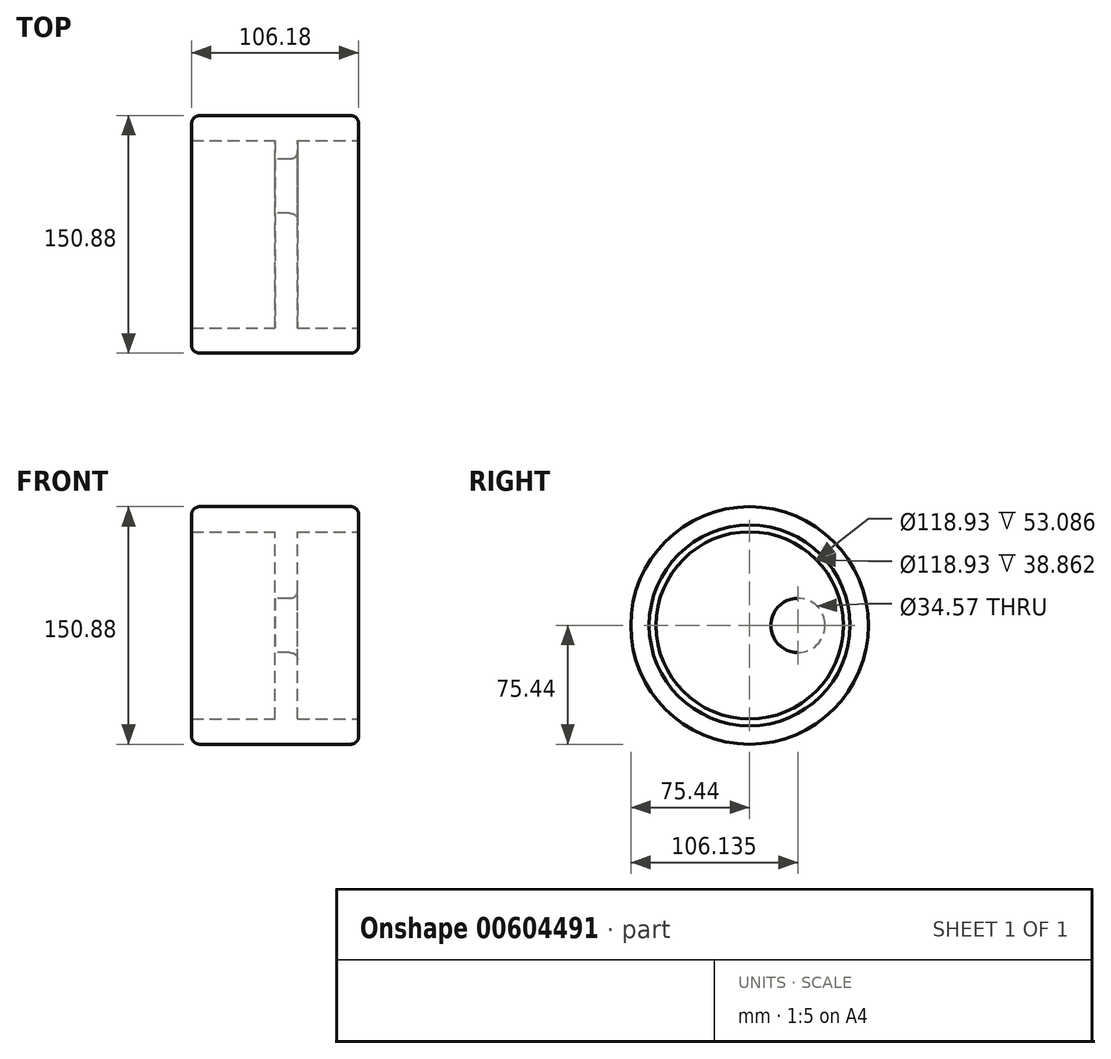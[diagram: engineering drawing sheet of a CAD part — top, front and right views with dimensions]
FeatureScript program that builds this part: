
annotation { "Feature Type Name" : "Feature", "Feature Type Description" : "" }
export const myFeature = defineFeature(function(context is Context, id is Id, definition is map)
    precondition{}
    {
        {
            var Q0;
            Q0=qCreatedBy(makeId("Right.planeOp"),FACE);
            var sketch = newSketch(context, id + "F0", { "sketchPlane" : qUnion([Q0])});
            skCircle(sketch, "E0", {"center": v(0, 0) * mm, "radius": 75.44 * mm});
            skSolve(sketch);
        }
        {
            var Q0;
            Q0 = qSketchRegion(id + "F0", true);
            extrude(context, id + "F1", {"entities" : qUnion([Q0]), "endBound" : BoundingType.SYMMETRIC, "depth" : 106.17 * mm, "offsetDistance" : 25.4 * mm});
        }
        {
            var Q0;
            Q0=makeQuery(id+"F1.opExtrude","SWEPT_FACE",FACE,{"disambiguationData":[OSD([sQuery(id+"F0.wireOp",EDGE,"E0")])]});
            fillet(context, id + "F2", {"entities" : qUnion([Q0]), "radius" : 5.08 * mm, "tangentPropagation" : true, "allowEdgeOverflow" : false});
        }
        {
            var Q0;
            Q0=qCreatedBy(makeId("Right.planeOp"),FACE);
            var sketch = newSketch(context, id + "F3", { "sketchPlane" : qUnion([Q0])});
            skCircle(sketch, "E1", {"center": v(0, 0) * mm, "radius": 58.8 * mm});
            skSolve(sketch);
        }
        {
            var Q0;
            Q0 = qSketchRegion(id + "F3", true);
            extrude(context, id + "F4", {"entities" : qUnion([Q0]), "operationType" : NewBodyOperationType.REMOVE, "endBound" : BoundingType.SYMMETRIC, "oppositeDirection" : true, "depth" : 134.62 * mm, "offsetDistance" : 25.4 * mm});
        }
        {
            var Q0;
            Q0=makeQuery(id+"F4.boolean.opBoolean","INTERSECT",EDGE,{"derivedFrom":[makeQuery(id+"F1.opExtrude","CAP_FACE",FACE,{"disambiguationData":[OSD([sQuery(id+"F0.wireOp",EDGE,"E0")])],"isStart":true}),makeQuery(id+"F4.opExtrude","SWEPT_FACE",FACE,{"disambiguationData":[OSD([sQuery(id+"F3.wireOp",EDGE,"E1")])]})]});
            var Q1;
            Q1=makeQuery(id+"F4.boolean.opBoolean","INTERSECT",EDGE,{"derivedFrom":[makeQuery(id+"F1.opExtrude","CAP_FACE",FACE,{"disambiguationData":[OSD([sQuery(id+"F0.wireOp",EDGE,"E0")])],"isStart":false}),makeQuery(id+"F4.opExtrude","SWEPT_FACE",FACE,{"disambiguationData":[OSD([sQuery(id+"F3.wireOp",EDGE,"E1")])]})]});
            fillet(context, id + "F5", {"entities" : qUnion([Q0, Q1]), "radius" : 5.08 * mm, "tangentPropagation" : true, "allowEdgeOverflow" : false});
        }
        {
            var Q0;
            Q0=qCreatedBy(makeId("Right.planeOp"),FACE);
            var sketch = newSketch(context, id + "F6", { "sketchPlane" : qUnion([Q0])});
            skCircle(sketch, "E2", {"center": v(0, 0) * mm, "radius": 63.75 * mm});
            skSolve(sketch);
        }
        {
            var Q0;
            Q0 = qSketchRegion(id + "F6", true);
            extrude(context, id + "F7", {"entities" : qUnion([Q0]), "operationType" : NewBodyOperationType.ADD, "endBound" : BoundingType.SYMMETRIC, "depth" : 106.17 * mm, "offsetDistance" : 25.4 * mm});
        }
        {
            var Q0;
            Q0=qCreatedBy(makeId("Right.planeOp"),FACE);
            var sketch = newSketch(context, id + "F8", { "sketchPlane" : qUnion([Q0])});
            skCircle(sketch, "E3", {"center": v(0, 0) * mm, "radius": 59.46 * mm});
            skSolve(sketch);
        }
        {
            var Q0;
            Q0 = qSketchRegion(id + "F8", true);
            extrude(context, id + "F9", {"entities" : qUnion([Q0]), "operationType" : NewBodyOperationType.REMOVE, "endBound" : BoundingType.SYMMETRIC, "oppositeDirection" : true, "depth" : 167.64 * mm, "offsetDistance" : 25.4 * mm});
        }
        {
            var Q0;
            Q0=qCreatedBy(makeId("Right.planeOp"),FACE);
            var sketch = newSketch(context, id + "F10", { "sketchPlane" : qUnion([Q0])});
            skCircle(sketch, "E4", {"center": v(0, 0) * mm, "radius": 60.4 * mm});
            skSolve(sketch);
        }
        {
            var Q0;
            Q0 = qSketchRegion(id + "F10", true);
            extrude(context, id + "F11", {"entities" : qUnion([Q0]), "operationType" : NewBodyOperationType.ADD, "depth" : 14.22 * mm, "offsetDistance" : 25.4 * mm});
        }
        {
            var Q0;
            Q0=makeQuery(id+"F11.opExtrude","CAP_FACE",FACE,{"disambiguationData":[OSD([sQuery(id+"F10.wireOp",EDGE,"E4")])],"isStart":true});
            var sketch = newSketch(context, id + "F12", { "sketchPlane" : qUnion([Q0])});
            skCircle(sketch, "E5", {"center": v(-30.7, 0) * mm, "radius": 17.29 * mm});
            skSolve(sketch);
        }
        {
            var Q0;
            Q0 = qSketchRegion(id + "F12", true);
            extrude(context, id + "F13", {"entities" : qUnion([Q0]), "operationType" : NewBodyOperationType.REMOVE, "oppositeDirection" : true, "depth" : 25.4 * mm, "offsetDistance" : 25.4 * mm});
        }
        {
            var Q0;
            Q0=makeQuery(id+"F13.boolean.opBoolean","COPY",EDGE,{"derivedFrom":makeQuery(id+"F13.opExtrude","CAP_EDGE",EDGE,{"disambiguationData":[OSD([sQuery(id+"F12.wireOp",EDGE,"E5")])],"isStart":true})});
            var Q1;
            Q1=makeQuery(id+"F13.boolean.opBoolean","INTERSECT",EDGE,{"derivedFrom":[makeQuery(id+"F11.opExtrude","CAP_FACE",FACE,{"disambiguationData":[OSD([sQuery(id+"F10.wireOp",EDGE,"E4")])],"isStart":false}),makeQuery(id+"F13.opExtrude","SWEPT_FACE",FACE,{"disambiguationData":[OSD([sQuery(id+"F12.wireOp",EDGE,"E5")])]})]});
            fillet(context, id + "F14", {"entities" : qUnion([Q0, Q1]), "radius" : 5.08 * mm, "tangentPropagation" : true, "rho" : 0.5, "crossSection" : FilletCrossSection.CONIC, "allowEdgeOverflow" : false});
        }
    });
